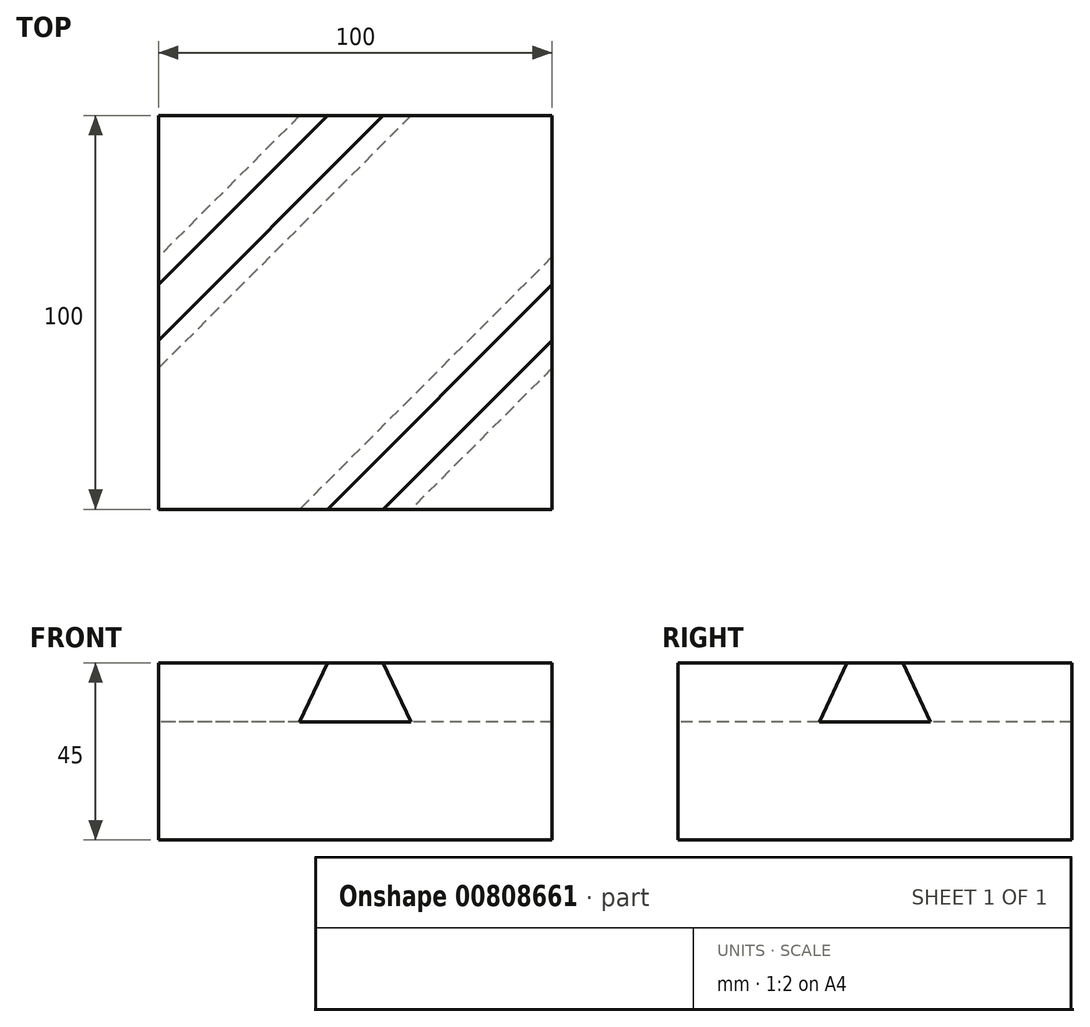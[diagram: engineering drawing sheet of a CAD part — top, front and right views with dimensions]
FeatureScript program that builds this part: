
annotation { "Feature Type Name" : "Feature", "Feature Type Description" : "" }
export const myFeature = defineFeature(function(context is Context, id is Id, definition is map)
    precondition{}
    {
        {
            var Q0;
            Q0=qCreatedBy(makeId("Top.planeOp"),FACE);
            var sketch = newSketch(context, id + "F0", { "sketchPlane" : qUnion([Q0])});
            skLineSegment(sketch, "E0.bottom", {"start": v(50, 50) * mm, "end": v(-50, 50) * mm});
            skLineSegment(sketch, "E0.top", {"start": v(50, -50) * mm, "end": v(-50, -50) * mm});
            skLineSegment(sketch, "E0.left", {"start": v(50, 50) * mm, "end": v(50, -50) * mm});
            skLineSegment(sketch, "E0.right", {"start": v(-50, 50) * mm, "end": v(-50, -50) * mm});
            skPoint(sketch, "E0.middle", {"position": v(0, 0) * mm});
            skSolve(sketch);
        }
        {
            var Q0;
            Q0 = qSketchRegion(id + "F0", true);
            extrude(context, id + "F1", {"entities" : qUnion([Q0]), "depth" : 45 * mm, "offsetDistance" : 25 * mm});
        }
        {
            var Q0;
            Q0=makeQuery(id+"F1.opExtrude","CAP_FACE",FACE,{"disambiguationData":[OSD([sQuery(id+"F0.wireOp",EDGE,"E0.bottom"),sQuery(id+"F0.wireOp",EDGE,"E0.top"),sQuery(id+"F0.wireOp",EDGE,"E0.left"),sQuery(id+"F0.wireOp",EDGE,"E0.right")])],"isStart":false});
            cPlane(context, id + "F2", {"entities" : qUnion([Q0]), "cplaneType" : CPlaneType.OFFSET, "offset" : 15 * mm, "oppositeDirection" : true, "width" : 150 * mm, "height" : 150 * mm});
        }
        {
            var Q0;
            Q0=qCreatedBy(id+"F2.planeOp",FACE);
            var sketch = newSketch(context, id + "F3", { "sketchPlane" : qUnion([Q0])});
            skLineSegment(sketch, "E1.bottom", {"start": v(50, 50) * mm, "end": v(-50, 50) * mm, "construction": true});
            skLineSegment(sketch, "E1.top", {"start": v(50, -50) * mm, "end": v(-50, -50) * mm, "construction": true});
            skLineSegment(sketch, "E1.left", {"start": v(50, 50) * mm, "end": v(50, -50) * mm, "construction": true});
            skLineSegment(sketch, "E1.right", {"start": v(-50, 50) * mm, "end": v(-50, -50) * mm, "construction": true});
            skPoint(sketch, "E1.middle", {"position": v(0, 0) * mm});
            skLineSegment(sketch, "E2", {"start": v(0, 50) * mm, "end": v(-50, 0) * mm, "construction": true});
            skLineSegment(sketch, "E3", {"start": v(0, -50) * mm, "end": v(50, 0) * mm, "construction": true});
            skLineSegment(sketch, "E4.left", {"start": v(14.14, 50) * mm, "end": v(-50, -14.14) * mm});
            skLineSegment(sketch, "E4.right", {"start": v(-14.14, 50) * mm, "end": v(-50, 14.14) * mm});
            skPoint(sketch, "E4.middle", {"position": v(-25, 25) * mm});
            skLineSegment(sketch, "E5.left", {"start": v(50, -14.14) * mm, "end": v(14.14, -50) * mm});
            skLineSegment(sketch, "E5.right", {"start": v(50, 14.14) * mm, "end": v(-14.14, -50) * mm});
            skPoint(sketch, "E5.middle", {"position": v(25, -25) * mm});
            skPoint(sketch, "E4.top.end.orphan", {"position": v(-67.43, -3.28) * mm});
            skPoint(sketch, "E6.orphan", {"position": v(-53.28, -17.43) * mm});
            skPoint(sketch, "E5.top.end.orphan", {"position": v(-17.43, -53.28) * mm});
            skPoint(sketch, "E7.orphan", {"position": v(-3.28, -67.43) * mm});
            skPoint(sketch, "E8.orphan", {"position": v(53.28, 17.43) * mm});
            skPoint(sketch, "E9.orphan", {"position": v(67.43, 3.28) * mm});
            skPoint(sketch, "E10.orphan", {"position": v(3.28, 67.43) * mm});
            skPoint(sketch, "E11.orphan", {"position": v(17.43, 53.28) * mm});
            skLineSegment(sketch, "E12", {"start": v(-14.14, 50) * mm, "end": v(14.14, 50) * mm});
            skLineSegment(sketch, "E13", {"start": v(50, 14.14) * mm, "end": v(50, -14.14) * mm});
            skLineSegment(sketch, "E14", {"start": v(14.14, -50) * mm, "end": v(-14.14, -50) * mm});
            skLineSegment(sketch, "E15", {"start": v(-50, -14.14) * mm, "end": v(-50, 14.14) * mm});
            skSolve(sketch);
        }
        {
            var Q0;
            Q0=makeQuery(id+"F1.opExtrude","CAP_FACE",FACE,{"disambiguationData":[OSD([sQuery(id+"F0.wireOp",EDGE,"E0.bottom"),sQuery(id+"F0.wireOp",EDGE,"E0.top"),sQuery(id+"F0.wireOp",EDGE,"E0.left"),sQuery(id+"F0.wireOp",EDGE,"E0.right")])],"isStart":false});
            cPlane(context, id + "F4", {"entities" : qUnion([Q0]), "cplaneType" : CPlaneType.OFFSET, "offset" : 0 * mm, "oppositeDirection" : true, "width" : 150 * mm, "height" : 150 * mm});
        }
        {
            var Q0;
            Q0=qCreatedBy(id+"F4.planeOp",FACE);
            var sketch = newSketch(context, id + "F5", { "sketchPlane" : qUnion([Q0])});
            skLineSegment(sketch, "E16.bottom", {"start": v(50, 50) * mm, "end": v(-50, 50) * mm, "construction": true});
            skLineSegment(sketch, "E16.top", {"start": v(50, -50) * mm, "end": v(-50, -50) * mm, "construction": true});
            skLineSegment(sketch, "E16.left", {"start": v(50, 50) * mm, "end": v(50, -50) * mm, "construction": true});
            skLineSegment(sketch, "E16.right", {"start": v(-50, 50) * mm, "end": v(-50, -50) * mm, "construction": true});
            skPoint(sketch, "E16.middle", {"position": v(0, 0) * mm});
            skLineSegment(sketch, "E17", {"start": v(0, 50) * mm, "end": v(-50, 0) * mm, "construction": true});
            skLineSegment(sketch, "E18", {"start": v(0, -50) * mm, "end": v(50, 0) * mm, "construction": true});
            skLineSegment(sketch, "E19.left", {"start": v(-7.07, 50) * mm, "end": v(-50, 7.07) * mm});
            skLineSegment(sketch, "E19.right", {"start": v(7.07, 50) * mm, "end": v(-50, -7.07) * mm});
            skPoint(sketch, "E19.middle", {"position": v(-25, 25) * mm});
            skLineSegment(sketch, "E20.left", {"start": v(50, 7.07) * mm, "end": v(-7.07, -50) * mm});
            skLineSegment(sketch, "E20.right", {"start": v(50, -7.07) * mm, "end": v(7.07, -50) * mm});
            skPoint(sketch, "E20.middle", {"position": v(25, -25) * mm});
            skPoint(sketch, "E19.bottom.start.orphan", {"position": v(6.82, 63.9) * mm});
            skPoint(sketch, "E21.orphan", {"position": v(13.9, 56.82) * mm});
            skPoint(sketch, "E20.bottom.start.orphan", {"position": v(56.82, 13.9) * mm});
            skPoint(sketch, "E22.orphan", {"position": v(63.9, 6.82) * mm});
            skPoint(sketch, "E20.top.end.orphan", {"position": v(-6.82, -63.9) * mm});
            skPoint(sketch, "E23.orphan", {"position": v(-13.9, -56.82) * mm});
            skPoint(sketch, "E19.top.end.orphan", {"position": v(-56.82, -13.9) * mm});
            skPoint(sketch, "E24.orphan", {"position": v(-63.9, -6.82) * mm});
            skLineSegment(sketch, "E25", {"start": v(-50, 7.07) * mm, "end": v(-50, -7.07) * mm});
            skLineSegment(sketch, "E26", {"start": v(-7.07, -50) * mm, "end": v(7.07, -50) * mm});
            skLineSegment(sketch, "E27", {"start": v(50, -7.07) * mm, "end": v(50, 7.07) * mm});
            skLineSegment(sketch, "E28", {"start": v(-7.07, 50) * mm, "end": v(7.07, 50) * mm});
            skSolve(sketch);
        }
        {
            var Q0;
            Q0=makeQuery(id+"F5.imprint","IMPRINT",FACE,{"disambiguationData":[TD([[makeQuery(id+"F5.imprint","IMPRINT",EDGE,{"derivedFrom":sQuery(id+"F5.wireOp",EDGE,"E20.left")}),1.0]])]});
            var Q1;
            Q1=makeQuery(id+"F5.imprint","IMPRINT",FACE,{"disambiguationData":[TD([[makeQuery(id+"F5.imprint","IMPRINT",EDGE,{"derivedFrom":sQuery(id+"F5.wireOp",EDGE,"E19.left")}),1.0]])]});
            extrude(context, id + "F6", {"entities" : qUnion([Q0, Q1]), "operationType" : NewBodyOperationType.REMOVE, "oppositeDirection" : true, "depth" : 15 * mm, "offsetDistance" : 25 * mm});
        }
        {
            var Q1;
            Q1=makeQuery(id+"F3.imprint","IMPRINT",FACE,{"disambiguationData":[TD([[makeQuery(id+"F3.imprint","IMPRINT",EDGE,{"derivedFrom":sQuery(id+"F3.wireOp",EDGE,"E5.left")}),-1.0]])]});
            var Q2;
            Q2=makeQuery(id+"F5.imprint","IMPRINT",FACE,{"disambiguationData":[TD([[makeQuery(id+"F5.imprint","IMPRINT",EDGE,{"derivedFrom":sQuery(id+"F5.wireOp",EDGE,"E20.left")}),1.0]])]});
            loft(context, id + "F7", {"operationType" : NewBodyOperationType.REMOVE, "sheetProfilesArray" : [{ "sheetProfileEntities" : qUnion([Q1]) }, { "sheetProfileEntities" : qUnion([Q2]) }]});
        }
        {
            var Q1;
            Q1=makeQuery(id+"F3.imprint","IMPRINT",FACE,{"disambiguationData":[TD([[makeQuery(id+"F3.imprint","IMPRINT",EDGE,{"derivedFrom":sQuery(id+"F3.wireOp",EDGE,"E4.left")}),-1.0]])]});
            var Q2;
            Q2=makeQuery(id+"F5.imprint","IMPRINT",FACE,{"disambiguationData":[TD([[makeQuery(id+"F5.imprint","IMPRINT",EDGE,{"derivedFrom":sQuery(id+"F5.wireOp",EDGE,"E19.left")}),1.0]])]});
            loft(context, id + "F8", {"operationType" : NewBodyOperationType.REMOVE, "sheetProfilesArray" : [{ "sheetProfileEntities" : qUnion([Q1]) }, { "sheetProfileEntities" : qUnion([Q2]) }]});
        }
    });
